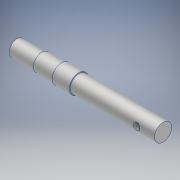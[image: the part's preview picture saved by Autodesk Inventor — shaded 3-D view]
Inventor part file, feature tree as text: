
AUTODESK INVENTOR PART (.ipt)
format: ipt  version: 2018 (Build 220112000, 112)  size: 136,704 bytes
history: native  units: mm
features: sketch x3, other x2, revolve x1, extrude x1, hole x1
ambient origin geometry x8: Origin, YZ Plane, XZ Plane, XY Plane, X Axis, Y Axis, Z Axis, Center Point
bodies: Body1 (feature_tree)
feature tree (8):
  other  "ソリッド1"
  revolve  "回転1"
  extrude  "押し出し2"  Depth=11.0mm
  other  "作業平面1"
  hole  "穴1"  [1 undecoded]
  sketch  "スケッチ1"
  sketch  "スケッチ2"
  sketch  "スケッチ3"
note: 1 required parameter value undecoded (feature->parameter linkage not recoverable at this tier; creation-order binding heuristic only, values carry confidence <= 0.55)
